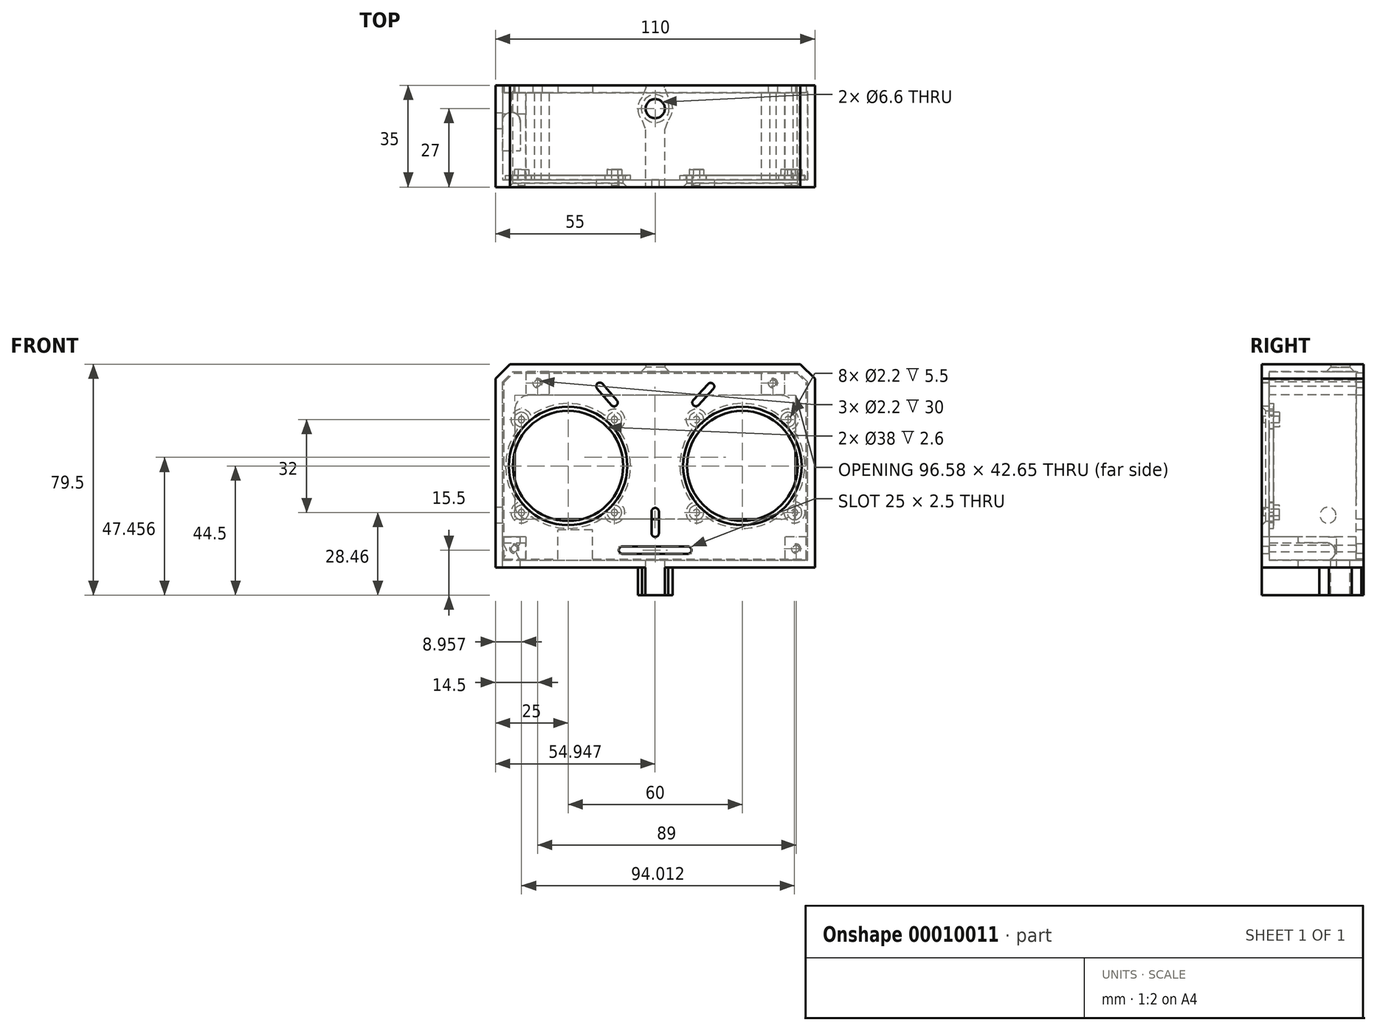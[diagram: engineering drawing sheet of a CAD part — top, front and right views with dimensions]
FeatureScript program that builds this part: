
annotation { "Feature Type Name" : "Feature", "Feature Type Description" : "" }
export const myFeature = defineFeature(function(context is Context, id is Id, definition is map)
    precondition{}
    {
        {
            var Q0;
            Q0=qCreatedBy(makeId("Front.planeOp"),FACE);
            var sketch = newSketch(context, id + "F0", { "sketchPlane" : qUnion([Q0])});
            skLineSegment(sketch, "E0.bottom", {"start": v(0, 0) * mm, "end": v(110, 0) * mm});
            skLineSegment(sketch, "E0.top", {"start": v(0, 70) * mm, "end": v(110, 70) * mm});
            skLineSegment(sketch, "E0.left", {"start": v(0, 0) * mm, "end": v(0, 70) * mm});
            skLineSegment(sketch, "E0.right", {"start": v(110, 0) * mm, "end": v(110, 70) * mm});
            skCircle(sketch, "E1", {"center": v(25, 35) * mm, "radius": 19 * mm});
            skCircle(sketch, "E2", {"center": v(85, 35) * mm, "radius": 19 * mm});
            skSolve(sketch);
        }
        {
            var Q0;
            Q0=makeQuery(id+"F0.imprint","IMPRINT",FACE,{"disambiguationData":[TD([[makeQuery(id+"F0.imprint","IMPRINT",EDGE,{"derivedFrom":sQuery(id+"F0.wireOp",EDGE,"E0.bottom")}),1.0]])]});
            extrude(context, id + "F1", {"entities" : qUnion([Q0]), "depth" : 35 * mm});
        }
        {
            var Q0;
            Q0=makeQuery(id+"F1.opExtrude","CAP_FACE",FACE,{"disambiguationData":[OSD([sQuery(id+"F0.wireOp",EDGE,"E0.bottom"),sQuery(id+"F0.wireOp",EDGE,"E0.top"),sQuery(id+"F0.wireOp",EDGE,"E0.left"),sQuery(id+"F0.wireOp",EDGE,"E0.right"),sQuery(id+"F0.wireOp",EDGE,"E1"),sQuery(id+"F0.wireOp",EDGE,"E2")])],"isStart":false});
            var sketch = newSketch(context, id + "F2", { "sketchPlane" : qUnion([Q0])});
            skCircle(sketch, "E3", {"center": v(8.96, 50.96) * mm, "radius": 1.1 * mm});
            skCircle(sketch, "E4", {"center": v(40.96, 50.96) * mm, "radius": 1.1 * mm});
            skCircle(sketch, "E5", {"center": v(69.22, 50.96) * mm, "radius": 1.1 * mm});
            skCircle(sketch, "E6", {"center": v(100.72, 50.96) * mm, "radius": 1.1 * mm});
            skCircle(sketch, "E7", {"center": v(69.22, 18.96) * mm, "radius": 1.1 * mm});
            skCircle(sketch, "E8", {"center": v(102.97, 18.96) * mm, "radius": 1.1 * mm});
            skCircle(sketch, "E9", {"center": v(8.96, 18.96) * mm, "radius": 1.1 * mm});
            skCircle(sketch, "E10", {"center": v(40.96, 18.96) * mm, "radius": 1.1 * mm});
            skSolve(sketch);
        }
        {
            var Q0;
            Q0=makeQuery(id+"F2.imprint","IMPRINT",FACE,{"disambiguationData":[TD([[makeQuery(id+"F2.imprint","IMPRINT",EDGE,{"derivedFrom":sQuery(id+"F2.wireOp",EDGE,"E3")}),1.0]])]});
            var Q1;
            Q1=makeQuery(id+"F2.imprint","IMPRINT",FACE,{"disambiguationData":[TD([[makeQuery(id+"F2.imprint","IMPRINT",EDGE,{"derivedFrom":sQuery(id+"F2.wireOp",EDGE,"E4")}),1.0]])]});
            var Q2;
            Q2=makeQuery(id+"F2.imprint","IMPRINT",FACE,{"disambiguationData":[TD([[makeQuery(id+"F2.imprint","IMPRINT",EDGE,{"derivedFrom":sQuery(id+"F2.wireOp",EDGE,"E5")}),1.0]])]});
            var Q3;
            Q3=makeQuery(id+"F2.imprint","IMPRINT",FACE,{"disambiguationData":[TD([[makeQuery(id+"F2.imprint","IMPRINT",EDGE,{"derivedFrom":sQuery(id+"F2.wireOp",EDGE,"E6")}),1.0]])]});
            var Q4;
            Q4=makeQuery(id+"F2.imprint","IMPRINT",FACE,{"disambiguationData":[TD([[makeQuery(id+"F2.imprint","IMPRINT",EDGE,{"derivedFrom":sQuery(id+"F2.wireOp",EDGE,"E7")}),1.0]])]});
            var Q5;
            Q5=makeQuery(id+"F2.imprint","IMPRINT",FACE,{"disambiguationData":[TD([[makeQuery(id+"F2.imprint","IMPRINT",EDGE,{"derivedFrom":sQuery(id+"F2.wireOp",EDGE,"E8")}),1.0]])]});
            var Q6;
            Q6=makeQuery(id+"F2.imprint","IMPRINT",FACE,{"disambiguationData":[TD([[makeQuery(id+"F2.imprint","IMPRINT",EDGE,{"derivedFrom":sQuery(id+"F2.wireOp",EDGE,"E9")}),1.0]])]});
            var Q7;
            Q7=makeQuery(id+"F2.imprint","IMPRINT",FACE,{"disambiguationData":[TD([[makeQuery(id+"F2.imprint","IMPRINT",EDGE,{"derivedFrom":sQuery(id+"F2.wireOp",EDGE,"E10")}),1.0]])]});
            extrude(context, id + "F3", {"entities" : qUnion([Q0, Q1, Q2, Q3, Q4, Q5, Q6, Q7]), "operationType" : NewBodyOperationType.REMOVE, "endBound" : BoundingType.THROUGH_ALL, "oppositeDirection" : true, "depth" : 25 * mm});
        }
        {
            var Q0;
            Q0=makeQuery(id+"F1.opExtrude","SWEPT_EDGE",EDGE,{"disambiguationData":[OSD([sQuery(id+"F0.wireOp",EDGE,"E0.top"),sQuery(id+"F0.wireOp",EDGE,"E0.right")])]});
            var Q1;
            Q1=makeQuery(id+"F1.opExtrude","SWEPT_EDGE",EDGE,{"disambiguationData":[OSD([sQuery(id+"F0.wireOp",EDGE,"E0.top"),sQuery(id+"F0.wireOp",EDGE,"E0.left")])]});
            chamfer(context, id + "F4", {"entities" : qUnion([Q0, Q1]), "width" : 5 * mm, "tangentPropagation" : true});
        }
        {
            var Q0;
            Q0=makeQuery(id+"F1.opExtrude","CAP_FACE",FACE,{"disambiguationData":[OSD([sQuery(id+"F0.wireOp",EDGE,"E0.bottom"),sQuery(id+"F0.wireOp",EDGE,"E0.top"),sQuery(id+"F0.wireOp",EDGE,"E0.left"),sQuery(id+"F0.wireOp",EDGE,"E0.right"),sQuery(id+"F0.wireOp",EDGE,"E1"),sQuery(id+"F0.wireOp",EDGE,"E2"),sQuery(id+"F0.wireOp",EDGE,"aa02c46e-2f35-42cb-8656-125fe3f55123.bottom"),sQuery(id+"F0.wireOp",EDGE,"aa02c46e-2f35-42cb-8656-125fe3f55123.top"),sQuery(id+"F0.wireOp",EDGE,"d7e0d663-ddb0-4fa4-9e14-f7d8174dc5fa.filletArc"),sQuery(id+"F0.wireOp",EDGE,"f2758223-459b-4cfb-ad80-82116a0456be.filletArc"),sQuery(id+"F0.wireOp",EDGE,"173b874d-1bc1-43cd-aeb1-c85f46f4946a.filletArc"),sQuery(id+"F0.wireOp",EDGE,"f53a1ce3-9789-4a8f-b4c7-98e42cb2f594.filletArc")])],"isStart":true});
            shell(context, id + "F5", {"entities" : qUnion([Q0]), "thickness" : 2.5 * mm});
        }
        {
            var Q0;
            {var subQ0=sQuery(id+"F0.wireOp",EDGE,"E0.bottom");var subQ1=sQuery(id+"F0.wireOp",EDGE,"E0.top");var subQ2=sQuery(id+"F0.wireOp",EDGE,"E0.left");var subQ3=sQuery(id+"F0.wireOp",EDGE,"E0.right");var subQ4=sQuery(id+"F0.wireOp",EDGE,"E1");var subQ5=sQuery(id+"F0.wireOp",EDGE,"E2");Q0=makeQuery(id+"F5.opShell","OFFSET_FACE",FACE,{"disambiguationData":[OSD([subQ0,subQ1,subQ2,subQ3,subQ4,subQ5]),TDD([makeQuery(id+"F1.opExtrude","CAP_FACE",FACE,{"disambiguationData":[OSD([subQ0,subQ1,subQ2,subQ3,subQ4,subQ5])],"isStart":true})]),OD(1.0)]});}
            var Q1;
            {var subQ0=sQuery(id+"F0.wireOp",EDGE,"E0.bottom");var subQ1=sQuery(id+"F0.wireOp",EDGE,"E0.top");var subQ2=sQuery(id+"F0.wireOp",EDGE,"E0.left");var subQ3=sQuery(id+"F0.wireOp",EDGE,"E0.right");var subQ4=sQuery(id+"F0.wireOp",EDGE,"E1");var subQ5=sQuery(id+"F0.wireOp",EDGE,"E2");Q1=makeQuery(id+"F5.opShell","OFFSET_FACE",FACE,{"disambiguationData":[OSD([subQ0,subQ1,subQ2,subQ3,subQ4,subQ5]),TDD([makeQuery(id+"F1.opExtrude","CAP_FACE",FACE,{"disambiguationData":[OSD([subQ0,subQ1,subQ2,subQ3,subQ4,subQ5])],"isStart":true})]),OD(0.0)]});}
            extrude(context, id + "F6", {"entities" : qUnion([Q0, Q1]), "operationType" : NewBodyOperationType.REMOVE, "oppositeDirection" : true, "depth" : 31 * mm});
        }
        {
            var Q0;
            Q0=makeQuery(id+"F5.opShell","OFFSET_FACE",FACE,{"disambiguationData":[OSD([sQuery(id+"F0.wireOp",EDGE,"E0.bottom")])]});
            var sketch = newSketch(context, id + "F7", { "sketchPlane" : qUnion([Q0])});
            skArc(sketch, "E11", {"start": v(58.29, -13.02) * mm, "mid": v(61, -7.99) * mm, "end": v(58.26, -2.97) * mm});
            skCircle(sketch, "E12", {"center": v(55, -8) * mm, "radius": 3.3 * mm});
            skLineSegment(sketch, "E13.left", {"start": v(58.29, -32.5) * mm, "end": v(58.29, -12.99) * mm});
            skLineSegment(sketch, "E13.right", {"start": v(51.66, -19.15) * mm, "end": v(51.66, -12.99) * mm});
            skLineSegment(sketch, "E14.left", {"start": v(58.26, -2.97) * mm, "end": v(58.26, 0) * mm});
            skLineSegment(sketch, "E14.right", {"start": v(51.8, -2.97) * mm, "end": v(51.8, 0) * mm});
            skLineSegment(sketch, "E15", {"start": v(58.26, 0) * mm, "end": v(51.8, 0) * mm});
            skArc(sketch, "E16.trimOffspring", {"start": v(51.8, -2.92) * mm, "mid": v(49, -7.92) * mm, "end": v(51.66, -12.99) * mm});
            skLineSegment(sketch, "E17", {"start": v(51.66, -19.15) * mm, "end": v(51.66, -35) * mm});
            skLineSegment(sketch, "E18", {"start": v(51.66, -35) * mm, "end": v(58.29, -35) * mm});
            skLineSegment(sketch, "E19", {"start": v(58.29, -35) * mm, "end": v(58.29, -32.5) * mm});
            skSolve(sketch);
        }
        {
            var Q0;
            Q0 = qSketchRegion(id + "F7", true);
            extrude(context, id + "F8", {"entities" : qUnion([Q0]), "operationType" : NewBodyOperationType.ADD, "oppositeDirection" : true, "depth" : 12 * mm});
        }
        {
            var Q0;
            Q0=makeQuery(id+"F8.opExtrude","SWEPT_EDGE",EDGE,{"disambiguationData":[OSD([sQuery(id+"F7.wireOp",EDGE,"E11"),sQuery(id+"F7.wireOp",EDGE,"E13.left")])]});
            var Q1;
            Q1=makeQuery(id+"F8.opExtrude","SWEPT_EDGE",EDGE,{"disambiguationData":[OSD([sQuery(id+"F7.wireOp",EDGE,"E13.right"),sQuery(id+"F7.wireOp",EDGE,"E16.trimOffspring")])]});
            var Q2;
            Q2=makeQuery(id+"F8.opExtrude","SWEPT_EDGE",EDGE,{"disambiguationData":[OSD([sQuery(id+"F7.wireOp",EDGE,"E14.right"),sQuery(id+"F7.wireOp",EDGE,"E16.trimOffspring")])]});
            var Q3;
            Q3=makeQuery(id+"F8.opExtrude","SWEPT_EDGE",EDGE,{"disambiguationData":[OSD([sQuery(id+"F7.wireOp",EDGE,"E11"),sQuery(id+"F7.wireOp",EDGE,"E14.left")])]});
            chamfer(context, id + "F9", {"entities" : qUnion([Q0, Q1, Q2, Q3]), "width" : 5 * mm, "tangentPropagation" : true});
        }
        {
            var Q0;
            Q0=makeQuery(id+"F1.opExtrude","CAP_FACE",FACE,{"disambiguationData":[OSD([sQuery(id+"F0.wireOp",EDGE,"E0.bottom"),sQuery(id+"F0.wireOp",EDGE,"E0.top"),sQuery(id+"F0.wireOp",EDGE,"E0.left"),sQuery(id+"F0.wireOp",EDGE,"E0.right"),sQuery(id+"F0.wireOp",EDGE,"E1"),sQuery(id+"F0.wireOp",EDGE,"E2")])],"isStart":false});
            var sketch = newSketch(context, id + "F10", { "sketchPlane" : qUnion([Q0])});
            skLineSegment(sketch, "E20.left", {"start": v(42.5, 6) * mm, "end": v(42.5, 6) * mm});
            skPoint(sketch, "E21.visualSharp", {"position": v(67.5, 4.75) * mm});
            skPoint(sketch, "E22.visualSharp", {"position": v(67.5, 7.25) * mm});
            skLineSegment(sketch, "E20.bottom", {"start": v(43.75, 7.25) * mm, "end": v(66.25, 7.25) * mm});
            skLineSegment(sketch, "E20.top", {"start": v(43.75, 4.75) * mm, "end": v(66.25, 4.75) * mm});
            skPoint(sketch, "E23.visualSharp", {"position": v(42.5, 7.25) * mm});
            skLineSegment(sketch, "E20.right", {"start": v(67.5, 6) * mm, "end": v(67.5, 6) * mm});
            skPoint(sketch, "E24.visualSharp", {"position": v(42.5, 4.75) * mm});
            skArc(sketch, "E22.filletArc", {"start": v(67.5, 6) * mm, "mid": v(67.13, 6.88) * mm, "end": v(66.25, 7.25) * mm});
            skArc(sketch, "E24.filletArc", {"start": v(42.5, 6) * mm, "mid": v(42.87, 5.12) * mm, "end": v(43.75, 4.75) * mm});
            skArc(sketch, "E21.filletArc", {"start": v(66.25, 4.75) * mm, "mid": v(67.13, 5.12) * mm, "end": v(67.5, 6) * mm});
            skArc(sketch, "E23.filletArc", {"start": v(43.75, 7.25) * mm, "mid": v(42.87, 6.88) * mm, "end": v(42.5, 6) * mm});
            skLineSegment(sketch, "E25.bottom", {"start": v(55, 20.55) * mm, "end": v(55, 20.55) * mm});
            skLineSegment(sketch, "E25.top", {"start": v(55, 10.55) * mm, "end": v(55, 10.55) * mm});
            skLineSegment(sketch, "E25.left", {"start": v(53.75, 19.3) * mm, "end": v(53.75, 11.8) * mm});
            skLineSegment(sketch, "E25.right", {"start": v(56.25, 19.3) * mm, "end": v(56.25, 11.8) * mm});
            skPoint(sketch, "E26.visualSharp", {"position": v(53.75, 20.55) * mm});
            skArc(sketch, "E26.filletArc", {"start": v(55, 20.55) * mm, "mid": v(54.12, 20.18) * mm, "end": v(53.75, 19.3) * mm});
            skPoint(sketch, "E27.visualSharp", {"position": v(56.25, 20.55) * mm});
            skArc(sketch, "E27.filletArc", {"start": v(56.25, 19.3) * mm, "mid": v(55.88, 20.18) * mm, "end": v(55, 20.55) * mm});
            skPoint(sketch, "E28.visualSharp", {"position": v(56.25, 10.55) * mm});
            skArc(sketch, "E28.filletArc", {"start": v(55, 10.55) * mm, "mid": v(55.88, 10.91) * mm, "end": v(56.25, 11.8) * mm});
            skPoint(sketch, "E29.visualSharp", {"position": v(53.75, 10.55) * mm});
            skArc(sketch, "E29.filletArc", {"start": v(53.75, 11.8) * mm, "mid": v(54.12, 10.91) * mm, "end": v(55, 10.55) * mm});
            skLineSegment(sketch, "E30", {"start": v(35, 61.65) * mm, "end": v(39.88, 55.95) * mm});
            skLineSegment(sketch, "E31", {"start": v(41.64, 55.81) * mm, "end": v(41.64, 55.81) * mm});
            skLineSegment(sketch, "E32", {"start": v(41.78, 57.58) * mm, "end": v(36.9, 63.27) * mm});
            skLineSegment(sketch, "E33", {"start": v(68.14, 55.91) * mm, "end": v(68.14, 55.91) * mm});
            skLineSegment(sketch, "E34", {"start": v(68.1, 57.65) * mm, "end": v(73.16, 63.18) * mm});
            skLineSegment(sketch, "E35", {"start": v(69.94, 55.96) * mm, "end": v(75, 61.49) * mm});
            skLineSegment(sketch, "E36", {"start": v(35.14, 63.4) * mm, "end": v(35.14, 63.4) * mm});
            skLineSegment(sketch, "E37", {"start": v(40.73, 62.28) * mm, "end": v(40.46, 62.6) * mm});
            skLineSegment(sketch, "E38", {"start": v(40.46, 62.6) * mm, "end": v(40.73, 62.83) * mm});
            skLineSegment(sketch, "E39", {"start": v(74.96, 63.22) * mm, "end": v(74.96, 63.22) * mm});
            skPoint(sketch, "E40.visualSharp", {"position": v(36.09, 64.22) * mm});
            skArc(sketch, "E40.filletArc", {"start": v(36.9, 63.27) * mm, "mid": v(36.05, 63.7) * mm, "end": v(35.14, 63.4) * mm});
            skPoint(sketch, "E41.newPointA", {"position": v(34.46, 62.83) * mm});
            skPoint(sketch, "E41.newPointB", {"position": v(34.46, 62.28) * mm});
            skArc(sketch, "E41.filletArc", {"start": v(35.14, 63.4) * mm, "mid": v(34.7, 62.56) * mm, "end": v(35, 61.65) * mm});
            skPoint(sketch, "E42.visualSharp", {"position": v(42.59, 56.63) * mm});
            skArc(sketch, "E42.filletArc", {"start": v(41.64, 55.81) * mm, "mid": v(42.07, 56.67) * mm, "end": v(41.78, 57.58) * mm});
            skPoint(sketch, "E43.visualSharp", {"position": v(40.7, 55) * mm});
            skArc(sketch, "E43.filletArc", {"start": v(39.88, 55.95) * mm, "mid": v(40.73, 55.52) * mm, "end": v(41.64, 55.81) * mm});
            skPoint(sketch, "E44.visualSharp", {"position": v(67.28, 56.76) * mm});
            skArc(sketch, "E44.filletArc", {"start": v(68.1, 57.65) * mm, "mid": v(67.77, 56.77) * mm, "end": v(68.14, 55.91) * mm});
            skPoint(sketch, "E45.visualSharp", {"position": v(69.06, 55) * mm});
            skArc(sketch, "E45.filletArc", {"start": v(68.14, 55.91) * mm, "mid": v(69.05, 55.55) * mm, "end": v(69.94, 55.96) * mm});
            skPoint(sketch, "E46.visualSharp", {"position": v(74.03, 64.13) * mm});
            skArc(sketch, "E46.filletArc", {"start": v(74.96, 63.22) * mm, "mid": v(74.05, 63.58) * mm, "end": v(73.16, 63.18) * mm});
            skPoint(sketch, "E47.visualSharp", {"position": v(75.81, 62.38) * mm});
            skArc(sketch, "E47.filletArc", {"start": v(75, 61.49) * mm, "mid": v(75.33, 62.36) * mm, "end": v(74.96, 63.22) * mm});
            skSolve(sketch);
        }
        {
            var Q0;
            Q0 = qSketchRegion(id + "F10", true);
            extrude(context, id + "F11", {"entities" : qUnion([Q0]), "operationType" : NewBodyOperationType.REMOVE, "endBound" : BoundingType.THROUGH_ALL, "oppositeDirection" : true, "depth" : 25 * mm});
        }
        {
            var Q0;
            {var subQ0=sQuery(id+"F0.wireOp",EDGE,"E0.bottom");var subQ1=sQuery(id+"F0.wireOp",EDGE,"E0.top");var subQ2=sQuery(id+"F0.wireOp",EDGE,"E0.left");var subQ3=sQuery(id+"F0.wireOp",EDGE,"E0.right");var subQ4=sQuery(id+"F0.wireOp",EDGE,"E1");var subQ5=sQuery(id+"F0.wireOp",EDGE,"E2");var subQ6=makeQuery(id+"F1.opExtrude","CAP_FACE",FACE,{"disambiguationData":[OSD([subQ0,subQ1,subQ2,subQ3,subQ4,subQ5])],"isStart":true});Q0=makeQuery(id+"F6.boolean.opBoolean","MERGE",FACE,{"derivedFrom":[makeQuery(id+"F5.opShell","OFFSET_FACE",FACE,{"disambiguationData":[OSD([subQ0,subQ1,subQ2,subQ3,subQ4,subQ5]),TDD([makeQuery(id+"F1.opExtrude","CAP_FACE",FACE,{"disambiguationData":[OSD([subQ0,subQ1,subQ2,subQ3,subQ4,subQ5])],"isStart":false})])]}),makeQuery(id+"F6.opExtrude","CAP_FACE",FACE,{"disambiguationData":[OSD([subQ0,subQ1,subQ2,subQ3,subQ4,subQ5]),TDD([makeQuery(id+"F5.opShell","OFFSET_FACE",FACE,{"disambiguationData":[OSD([subQ0,subQ1,subQ2,subQ3,subQ4,subQ5]),TDD([subQ6]),OD(0.0)]})])],"isStart":false}),makeQuery(id+"F6.opExtrude","CAP_FACE",FACE,{"disambiguationData":[OSD([subQ0,subQ1,subQ2,subQ3,subQ4,subQ5]),TDD([makeQuery(id+"F5.opShell","OFFSET_FACE",FACE,{"disambiguationData":[OSD([subQ0,subQ1,subQ2,subQ3,subQ4,subQ5]),TDD([subQ6]),OD(1.0)]})])],"isStart":false})]});}
            var sketch = newSketch(context, id + "F12", { "sketchPlane" : qUnion([Q0])});
            skLineSegment(sketch, "E48.bottom", {"start": v(-99.5, 67.5) * mm, "end": v(-91.5, 67.5) * mm});
            skLineSegment(sketch, "E48.top", {"start": v(-99.5, 59.5) * mm, "end": v(-91.5, 59.5) * mm});
            skLineSegment(sketch, "E48.left", {"start": v(-99.5, 67.5) * mm, "end": v(-99.5, 59.5) * mm});
            skLineSegment(sketch, "E48.right", {"start": v(-91.5, 67.5) * mm, "end": v(-91.5, 59.5) * mm});
            skLineSegment(sketch, "E49.right", {"start": v(-10.5, 67.52) * mm, "end": v(-10.5, 59.52) * mm});
            skLineSegment(sketch, "E49.left", {"start": v(-18.5, 67.52) * mm, "end": v(-18.5, 59.52) * mm});
            skLineSegment(sketch, "E49.top", {"start": v(-18.5, 59.52) * mm, "end": v(-10.5, 59.52) * mm});
            skLineSegment(sketch, "E49.bottom", {"start": v(-18.5, 67.52) * mm, "end": v(-10.5, 67.52) * mm});
            skLineSegment(sketch, "E50.right", {"start": v(-99.57, 10.62) * mm, "end": v(-99.57, 2.56) * mm});
            skLineSegment(sketch, "E50.left", {"start": v(-107.5, 10.62) * mm, "end": v(-107.5, 2.62) * mm});
            skLineSegment(sketch, "E50.top", {"start": v(-107.5, 2.62) * mm, "end": v(-99.5, 2.62) * mm});
            skLineSegment(sketch, "E50.bottom", {"start": v(-107.5, 10.62) * mm, "end": v(-99.57, 10.62) * mm});
            skLineSegment(sketch, "E51.right", {"start": v(-2.5, 10.5) * mm, "end": v(-2.5, 2.5) * mm});
            skLineSegment(sketch, "E51.left", {"start": v(-10.5, 10.5) * mm, "end": v(-10.5, 2.5) * mm});
            skLineSegment(sketch, "E51.top", {"start": v(-10.5, 2.5) * mm, "end": v(-2.5, 2.5) * mm});
            skLineSegment(sketch, "E51.bottom", {"start": v(-10.5, 10.5) * mm, "end": v(-2.5, 10.5) * mm});
            skCircle(sketch, "E52", {"center": v(-95.5, 63.5) * mm, "radius": 1.1 * mm});
            skCircle(sketch, "E53", {"center": v(-14.5, 63.5) * mm, "radius": 1.1 * mm});
            skCircle(sketch, "E54", {"center": v(-103.5, 6.5) * mm, "radius": 1.1 * mm});
            skCircle(sketch, "E55", {"center": v(-6.5, 6.5) * mm, "radius": 1.1 * mm});
            skSolve(sketch);
        }
        {
            var Q0;
            Q0 = qSketchRegion(id + "F12", true);
            extrude(context, id + "F13", {"entities" : qUnion([Q0]), "operationType" : NewBodyOperationType.ADD, "depth" : 30 * mm});
        }
        {
            var Q0;
            Q0=makeQuery(id+"F1.opExtrude","SWEPT_FACE",FACE,{"disambiguationData":[OSD([sQuery(id+"F0.wireOp",EDGE,"E0.bottom")])]});
            var sketch = newSketch(context, id + "F14", { "sketchPlane" : qUnion([Q0])});
            skCircle(sketch, "E56", {"center": v(55, 8) * mm, "radius": 3.3 * mm});
            skSolve(sketch);
        }
        {
            var Q0;
            Q0 = qSketchRegion(id + "F14", true);
            extrude(context, id + "F15", {"entities" : qUnion([Q0]), "operationType" : NewBodyOperationType.REMOVE, "endBound" : BoundingType.THROUGH_ALL, "oppositeDirection" : true, "depth" : 25 * mm});
        }
        {
            var Q0;
            Q0=makeQuery(id+"F13.opExtrude","CAP_FACE",FACE,{"disambiguationData":[OSD([sQuery(id+"F12.wireOp",EDGE,"E48.bottom"),sQuery(id+"F12.wireOp",EDGE,"E48.top"),sQuery(id+"F12.wireOp",EDGE,"E48.left"),sQuery(id+"F12.wireOp",EDGE,"E48.right"),sQuery(id+"F12.wireOp",EDGE,"E52")])],"isStart":false});
            var sketch = newSketch(context, id + "F16", { "sketchPlane" : qUnion([Q0])});
            skLineSegment(sketch, "E57.0", {"start": v(-6.24, 67) * mm, "end": v(-103.76, 67) * mm});
            skLineSegment(sketch, "E57.1", {"start": v(-3, 63.76) * mm, "end": v(-6.24, 67) * mm});
            skLineSegment(sketch, "E57.2", {"start": v(-3, 3) * mm, "end": v(-3, 63.76) * mm});
            skLineSegment(sketch, "E57.3", {"start": v(-3, 3) * mm, "end": v(-21.46, 3) * mm});
            skLineSegment(sketch, "E57.4", {"start": v(-107, 3) * mm, "end": v(-107, 63.76) * mm});
            skLineSegment(sketch, "E57.5", {"start": v(-103.76, 67) * mm, "end": v(-107, 63.76) * mm});
            skCircle(sketch, "E58", {"center": v(-95.5, 63.5) * mm, "radius": 1.6 * mm});
            skCircle(sketch, "E59", {"center": v(-103.5, 6.5) * mm, "radius": 1.6 * mm});
            skCircle(sketch, "E60", {"center": v(-6.5, 6.5) * mm, "radius": 1.6 * mm});
            skCircle(sketch, "E61", {"center": v(-14.5, 63.5) * mm, "radius": 1.6 * mm});
            skLineSegment(sketch, "E62.top", {"start": v(-33.46, 13) * mm, "end": v(-21.46, 13) * mm});
            skLineSegment(sketch, "E62.left", {"start": v(-33.46, 3) * mm, "end": v(-33.46, 13) * mm});
            skLineSegment(sketch, "E62.right", {"start": v(-21.46, 3) * mm, "end": v(-21.46, 13) * mm});
            skLineSegment(sketch, "E63.trimOffspring", {"start": v(-33.46, 3) * mm, "end": v(-107, 3) * mm});
            skLineSegment(sketch, "E64.bottom", {"start": v(-98.24, 16.63) * mm, "end": v(-11.66, 16.63) * mm});
            skLineSegment(sketch, "E64.top", {"start": v(-98.24, 59.28) * mm, "end": v(-11.66, 59.28) * mm});
            skLineSegment(sketch, "E64.left", {"start": v(-103.24, 54.28) * mm, "end": v(-103.24, 21.63) * mm});
            skLineSegment(sketch, "E64.right", {"start": v(-6.66, 54.28) * mm, "end": v(-6.66, 21.63) * mm});
            skPoint(sketch, "E65.visualSharp", {"position": v(-103.24, 59.28) * mm});
            skArc(sketch, "E65.filletArc", {"start": v(-98.24, 59.28) * mm, "mid": v(-101.77, 57.82) * mm, "end": v(-103.24, 54.28) * mm});
            skPoint(sketch, "E66.visualSharp", {"position": v(-103.24, 16.63) * mm});
            skArc(sketch, "E66.filletArc", {"start": v(-103.24, 21.63) * mm, "mid": v(-101.77, 18.1) * mm, "end": v(-98.24, 16.63) * mm});
            skPoint(sketch, "E67.visualSharp", {"position": v(-6.66, 59.28) * mm});
            skArc(sketch, "E67.filletArc", {"start": v(-6.66, 54.28) * mm, "mid": v(-8.12, 57.82) * mm, "end": v(-11.66, 59.28) * mm});
            skPoint(sketch, "E68.visualSharp", {"position": v(-6.66, 16.63) * mm});
            skArc(sketch, "E68.filletArc", {"start": v(-11.66, 16.63) * mm, "mid": v(-8.12, 18.1) * mm, "end": v(-6.66, 21.63) * mm});
            skSolve(sketch);
        }
        {
            var Q0;
            Q0=makeQuery(id+"F16.imprint","IMPRINT",FACE,{"disambiguationData":[TD([[makeQuery(id+"F16.imprint","IMPRINT",EDGE,{"derivedFrom":sQuery(id+"F16.wireOp",EDGE,"E58")}),-1.0]])]});
            var Q1;
            {var subQ7=sQuery(id+"F16.wireOp",EDGE,"E57.1");Q1=makeQuery(id+"F16.imprint","IMPRINT",FACE,{"disambiguationData":[TD([[makeQuery(id+"F16.imprint","IMPRINT",EDGE,{"derivedFrom":subQ7}),1.0]])]});}
            extrude(context, id + "F17", {"entities" : qUnion([Q0, Q1]), "depth" : 2.5 * mm});
        }
        {
            var Q0;
            Q0=makeQuery(id+"F13.opExtrude","SWEPT_FACE",FACE,{"disambiguationData":[OSD([sQuery(id+"F12.wireOp",EDGE,"E51.bottom")])]});
            var sketch = newSketch(context, id + "F18", { "sketchPlane" : qUnion([Q0])});
            skLineSegment(sketch, "E69.bottom", {"start": v(5.5, -9.24) * mm, "end": v(5.5, -9.24) * mm});
            skLineSegment(sketch, "E69.top", {"start": v(2.5, -22.5) * mm, "end": v(8.5, -22.5) * mm});
            skLineSegment(sketch, "E69.left", {"start": v(2.5, -12.24) * mm, "end": v(2.5, -22.5) * mm});
            skLineSegment(sketch, "E69.right", {"start": v(8.5, -12.24) * mm, "end": v(8.5, -22.5) * mm});
            skPoint(sketch, "E70.visualSharp", {"position": v(8.5, -9.24) * mm});
            skArc(sketch, "E70.filletArc", {"start": v(8.5, -12.24) * mm, "mid": v(7.62, -10.12) * mm, "end": v(5.5, -9.24) * mm});
            skPoint(sketch, "E71.visualSharp", {"position": v(2.5, -9.24) * mm});
            skArc(sketch, "E71.filletArc", {"start": v(5.5, -9.24) * mm, "mid": v(3.38, -10.12) * mm, "end": v(2.5, -12.24) * mm});
            skSolve(sketch);
        }
        {
            var Q0;
            Q0 = qSketchRegion(id + "F18", true);
            extrude(context, id + "F19", {"entities" : qUnion([Q0]), "operationType" : NewBodyOperationType.REMOVE, "endBound" : BoundingType.UP_TO_NEXT, "oppositeDirection" : true, "depth" : 6 * mm});
        }
        {
            var Q0;
            Q0=makeQuery(id+"F13.opExtrude","SWEPT_FACE",FACE,{"disambiguationData":[OSD([sQuery(id+"F12.wireOp",EDGE,"E51.left")])]});
            var sketch = newSketch(context, id + "F20", { "sketchPlane" : qUnion([Q0])});
            skLineSegment(sketch, "E72.bottom", {"start": v(-32.5, 8.5) * mm, "end": v(-12.81, 8.5) * mm});
            skLineSegment(sketch, "E72.top", {"start": v(-32.5, 2.5) * mm, "end": v(-12.81, 2.5) * mm});
            skLineSegment(sketch, "E72.left", {"start": v(-32.5, 8.5) * mm, "end": v(-32.5, 2.5) * mm});
            skLineSegment(sketch, "E72.right", {"start": v(-9.81, 5.5) * mm, "end": v(-9.81, 5.5) * mm});
            skPoint(sketch, "E73.visualSharp", {"position": v(-9.81, 8.5) * mm});
            skArc(sketch, "E73.filletArc", {"start": v(-9.81, 5.5) * mm, "mid": v(-10.69, 7.63) * mm, "end": v(-12.81, 8.5) * mm});
            skPoint(sketch, "E74.visualSharp", {"position": v(-9.81, 2.5) * mm});
            skArc(sketch, "E74.filletArc", {"start": v(-12.81, 2.5) * mm, "mid": v(-10.69, 3.39) * mm, "end": v(-9.81, 5.5) * mm});
            skSolve(sketch);
        }
        {
            var Q0;
            Q0=makeQuery(id+"F20.imprint","IMPRINT",FACE,{"disambiguationData":[TD([[makeQuery(id+"F20.imprint","IMPRINT",EDGE,{"derivedFrom":sQuery(id+"F20.wireOp",EDGE,"E72.bottom")}),-1.0]])]});
            var Q1;
            Q1=makeQuery(id+"F5.opShell","OFFSET_FACE",FACE,{"disambiguationData":[OSD([sQuery(id+"F0.wireOp",EDGE,"E0.left")])]});
            extrude(context, id + "F21", {"entities" : qUnion([Q0]), "operationType" : NewBodyOperationType.REMOVE, "endBound" : BoundingType.UP_TO_SURFACE, "oppositeDirection" : true, "endBoundEntityFace" : qUnion([Q1]), "depth" : 25 * mm});
        }
        {
            var Q0;
            Q0=makeQuery(id+"F1.opExtrude","CAP_FACE",FACE,{"disambiguationData":[OSD([sQuery(id+"F0.wireOp",EDGE,"E0.bottom"),sQuery(id+"F0.wireOp",EDGE,"E0.top"),sQuery(id+"F0.wireOp",EDGE,"E0.left"),sQuery(id+"F0.wireOp",EDGE,"E0.right"),sQuery(id+"F0.wireOp",EDGE,"E1"),sQuery(id+"F0.wireOp",EDGE,"E2")])],"isStart":false});
            var sketch = newSketch(context, id + "F22", { "sketchPlane" : qUnion([Q0])});
            skCircle(sketch, "E75", {"center": v(8.96, 50.96) * mm, "radius": 1.1 * mm});
            skCircle(sketch, "E76", {"center": v(40.96, 50.96) * mm, "radius": 1.1 * mm});
            skCircle(sketch, "E77", {"center": v(8.96, 18.96) * mm, "radius": 1.1 * mm});
            skCircle(sketch, "E78", {"center": v(40.96, 18.96) * mm, "radius": 1.1 * mm});
            skCircle(sketch, "E79", {"center": v(69.22, 18.96) * mm, "radius": 1.1 * mm});
            skCircle(sketch, "E80", {"center": v(69.22, 50.96) * mm, "radius": 1.1 * mm});
            skCircle(sketch, "E81", {"center": v(100.72, 50.96) * mm, "radius": 1.1 * mm});
            skCircle(sketch, "E82", {"center": v(102.97, 18.96) * mm, "radius": 1.1 * mm});
            skSolve(sketch);
        }
        {
            var Q0;
            Q0=makeQuery(id+"F22.imprint","IMPRINT",FACE,{"disambiguationData":[TD([[makeQuery(id+"F22.imprint","IMPRINT",EDGE,{"derivedFrom":sQuery(id+"F22.wireOp",EDGE,"E76")}),1.0]])]});
            var Q1;
            Q1=makeQuery(id+"F22.imprint","IMPRINT",FACE,{"disambiguationData":[TD([[makeQuery(id+"F22.imprint","IMPRINT",EDGE,{"derivedFrom":sQuery(id+"F22.wireOp",EDGE,"E77")}),1.0]])]});
            var Q2;
            Q2=makeQuery(id+"F22.imprint","IMPRINT",FACE,{"disambiguationData":[TD([[makeQuery(id+"F22.imprint","IMPRINT",EDGE,{"derivedFrom":sQuery(id+"F22.wireOp",EDGE,"E81")}),1.0]])]});
            var Q3;
            Q3=makeQuery(id+"F22.imprint","IMPRINT",FACE,{"disambiguationData":[TD([[makeQuery(id+"F22.imprint","IMPRINT",EDGE,{"derivedFrom":sQuery(id+"F22.wireOp",EDGE,"E82")}),1.0]])]});
            var Q4;
            Q4=makeQuery(id+"F22.imprint","IMPRINT",FACE,{"disambiguationData":[TD([[makeQuery(id+"F22.imprint","IMPRINT",EDGE,{"derivedFrom":makeQuery(id+"F3.boolean.opBoolean","COPY",EDGE,{"derivedFrom":makeQuery(id+"F3.opExtrude","CAP_EDGE",EDGE,{"disambiguationData":[OSD([sQuery(id+"F2.wireOp",EDGE,"E3")])],"isStart":true})})}),1.0]])]});
            var Q5;
            Q5=makeQuery(id+"F22.imprint","IMPRINT",FACE,{"disambiguationData":[TD([[makeQuery(id+"F22.imprint","IMPRINT",EDGE,{"derivedFrom":makeQuery(id+"F3.boolean.opBoolean","COPY",EDGE,{"derivedFrom":makeQuery(id+"F3.opExtrude","CAP_EDGE",EDGE,{"disambiguationData":[OSD([sQuery(id+"F2.wireOp",EDGE,"E5")])],"isStart":true})})}),1.0]])]});
            var Q6;
            Q6=makeQuery(id+"F22.imprint","IMPRINT",FACE,{"disambiguationData":[TD([[makeQuery(id+"F22.imprint","IMPRINT",EDGE,{"derivedFrom":makeQuery(id+"F3.boolean.opBoolean","COPY",EDGE,{"derivedFrom":makeQuery(id+"F3.opExtrude","CAP_EDGE",EDGE,{"disambiguationData":[OSD([sQuery(id+"F2.wireOp",EDGE,"E7")])],"isStart":true})})}),1.0]])]});
            var Q7;
            Q7=makeQuery(id+"F22.imprint","IMPRINT",FACE,{"disambiguationData":[TD([[makeQuery(id+"F22.imprint","IMPRINT",EDGE,{"derivedFrom":makeQuery(id+"F3.boolean.opBoolean","COPY",EDGE,{"derivedFrom":makeQuery(id+"F3.opExtrude","CAP_EDGE",EDGE,{"disambiguationData":[OSD([sQuery(id+"F2.wireOp",EDGE,"E10")])],"isStart":true})})}),1.0]])]});
            var Q8;
            Q8=makeQuery(id+"F22.imprint","IMPRINT",FACE,{"disambiguationData":[TD([[makeQuery(id+"F22.imprint","IMPRINT",EDGE,{"derivedFrom":sQuery(id+"F22.wireOp",EDGE,"E75")}),1.0]])]});
            var Q9;
            Q9=makeQuery(id+"F22.imprint","IMPRINT",FACE,{"disambiguationData":[TD([[makeQuery(id+"F22.imprint","IMPRINT",EDGE,{"derivedFrom":sQuery(id+"F22.wireOp",EDGE,"E78")}),1.0]])]});
            var Q10;
            Q10=makeQuery(id+"F22.imprint","IMPRINT",FACE,{"disambiguationData":[TD([[makeQuery(id+"F22.imprint","IMPRINT",EDGE,{"derivedFrom":sQuery(id+"F22.wireOp",EDGE,"E79")}),1.0]])]});
            var Q11;
            Q11=makeQuery(id+"F22.imprint","IMPRINT",FACE,{"disambiguationData":[TD([[makeQuery(id+"F22.imprint","IMPRINT",EDGE,{"derivedFrom":sQuery(id+"F22.wireOp",EDGE,"E80")}),1.0]])]});
            extrude(context, id + "F23", {"entities" : qUnion([Q0, Q1, Q2, Q3, Q4, Q5, Q6, Q7, Q8, Q9, Q10, Q11]), "operationType" : NewBodyOperationType.ADD, "oppositeDirection" : true, "depth" : .5 * mm});
        }
        {
            var Q0;
            Q0=makeQuery(id+"F15.boolean.opBoolean","INTERSECT",EDGE,{"derivedFrom":[makeQuery(id+"F5.opShell","OFFSET_FACE",FACE,{"disambiguationData":[OSD([sQuery(id+"F0.wireOp",EDGE,"E0.top")])]}),makeQuery(id+"F15.opExtrude","SWEPT_FACE",FACE,{"disambiguationData":[OSD([sQuery(id+"F14.wireOp",EDGE,"E56")])]})]});
            chamfer(context, id + "F24", {"entities" : qUnion([Q0]), "width" : 1.5 * mm, "tangentPropagation" : true});
        }
        {
            var Q0;
            Q0=makeQuery(id+"F11.boolean.opBoolean","COPY",EDGE,{"derivedFrom":makeQuery(id+"F11.opExtrude","CAP_EDGE",EDGE,{"disambiguationData":[OSD([sQuery(id+"F10.wireOp",EDGE,"E32")])],"isStart":true})});
            var Q1;
            Q1=makeQuery(id+"F11.boolean.opBoolean","COPY",EDGE,{"derivedFrom":makeQuery(id+"F11.opExtrude","CAP_EDGE",EDGE,{"disambiguationData":[OSD([sQuery(id+"F10.wireOp",EDGE,"E35")])],"isStart":true})});
            var Q2;
            Q2=makeQuery(id+"F1.opExtrude","CAP_EDGE",EDGE,{"disambiguationData":[OSD([sQuery(id+"F0.wireOp",EDGE,"E1")])],"isStart":false});
            var Q3;
            Q3=makeQuery(id+"F1.opExtrude","CAP_EDGE",EDGE,{"disambiguationData":[OSD([sQuery(id+"F0.wireOp",EDGE,"E2")])],"isStart":false});
            var Q4;
            Q4=makeQuery(id+"F11.boolean.opBoolean","COPY",EDGE,{"derivedFrom":makeQuery(id+"F11.opExtrude","CAP_EDGE",EDGE,{"disambiguationData":[OSD([sQuery(id+"F10.wireOp",EDGE,"E25.right")])],"isStart":true})});
            var Q5;
            Q5=makeQuery(id+"F11.boolean.opBoolean","COPY",EDGE,{"derivedFrom":makeQuery(id+"F11.opExtrude","CAP_EDGE",EDGE,{"disambiguationData":[OSD([sQuery(id+"F10.wireOp",EDGE,"E20.bottom")])],"isStart":true})});
            chamfer(context, id + "F25", {"entities" : qUnion([Q0, Q1, Q2, Q3, Q4, Q5]), "width" : 1.4 * mm, "tangentPropagation" : true});
        }
        {
            var Q0;
            Q0=makeQuery(id+"F1.opExtrude","SWEPT_FACE",FACE,{"disambiguationData":[OSD([sQuery(id+"F0.wireOp",EDGE,"E0.left")])]});
            var sketch = newSketch(context, id + "F26", { "sketchPlane" : qUnion([Q0])});
            skCircle(sketch, "E83", {"center": v(12.25, 18) * mm, "radius": 2.75 * mm});
            skSolve(sketch);
        }
        {
            var Q0;
            Q0 = qSketchRegion(id + "F26", true);
            extrude(context, id + "F27", {"entities" : qUnion([Q0]), "operationType" : NewBodyOperationType.REMOVE, "oppositeDirection" : true, "depth" : 5 * mm});
        }
        {
            var Q0;
            {var subQ0=sQuery(id+"F0.wireOp",EDGE,"E0.bottom");var subQ1=sQuery(id+"F0.wireOp",EDGE,"E0.top");var subQ2=sQuery(id+"F0.wireOp",EDGE,"E0.left");var subQ3=sQuery(id+"F0.wireOp",EDGE,"E0.right");var subQ4=sQuery(id+"F0.wireOp",EDGE,"E1");var subQ5=sQuery(id+"F0.wireOp",EDGE,"E2");Q0=makeQuery(id+"F6.boolean.opBoolean","COPY",FACE,{"derivedFrom":makeQuery(id+"F6.opExtrude","CAP_FACE",FACE,{"disambiguationData":[OSD([subQ0,subQ1,subQ2,subQ3,subQ4,subQ5]),TDD([makeQuery(id+"F5.opShell","OFFSET_FACE",FACE,{"disambiguationData":[OSD([subQ0,subQ1,subQ2,subQ3,subQ4,subQ5]),TDD([makeQuery(id+"F1.opExtrude","CAP_FACE",FACE,{"disambiguationData":[OSD([subQ0,subQ1,subQ2,subQ3,subQ4,subQ5])],"isStart":true})]),OD(1.0)]})])],"isStart":false})});}
            var sketch = newSketch(context, id + "F28", { "sketchPlane" : qUnion([Q0])});
            skCircle(sketch, "E84", {"center": v(-69.22, 50.96) * mm, "radius": 2.5 * mm});
            skCircle(sketch, "E85", {"center": v(-69.22, 50.96) * mm, "radius": 1.1 * mm});
            skCircle(sketch, "E86", {"center": v(-100.72, 50.96) * mm, "radius": 2.5 * mm});
            skCircle(sketch, "E87", {"center": v(-100.72, 50.96) * mm, "radius": 1.1 * mm});
            skCircle(sketch, "E88", {"center": v(-69.22, 18.96) * mm, "radius": 2.5 * mm});
            skCircle(sketch, "E89", {"center": v(-69.22, 18.96) * mm, "radius": 1.1 * mm});
            skCircle(sketch, "E90", {"center": v(-102.97, 18.96) * mm, "radius": 2.5 * mm});
            skCircle(sketch, "E91", {"center": v(-102.97, 18.96) * mm, "radius": 1.1 * mm});
            skCircle(sketch, "E92", {"center": v(-40.96, 50.96) * mm, "radius": 2.5 * mm});
            skCircle(sketch, "E93", {"center": v(-40.96, 50.96) * mm, "radius": 1.1 * mm});
            skCircle(sketch, "E94", {"center": v(-8.96, 18.96) * mm, "radius": 1.1 * mm});
            skCircle(sketch, "E95", {"center": v(-40.96, 18.96) * mm, "radius": 1.1 * mm});
            skCircle(sketch, "E96", {"center": v(-8.96, 50.96) * mm, "radius": 2.5 * mm});
            skCircle(sketch, "E97", {"center": v(-8.96, 50.96) * mm, "radius": 1.1 * mm});
            skCircle(sketch, "E98", {"center": v(-8.96, 18.96) * mm, "radius": 2.5 * mm});
            skCircle(sketch, "E99", {"center": v(-40.96, 18.96) * mm, "radius": 2.5 * mm});
            skSolve(sketch);
        }
        {
            var Q0;
            Q0 = qSketchRegion(id + "F28", true);
            extrude(context, id + "F29", {"entities" : qUnion([Q0]), "operationType" : NewBodyOperationType.ADD, "depth" : 2 * mm});
        }
    });
